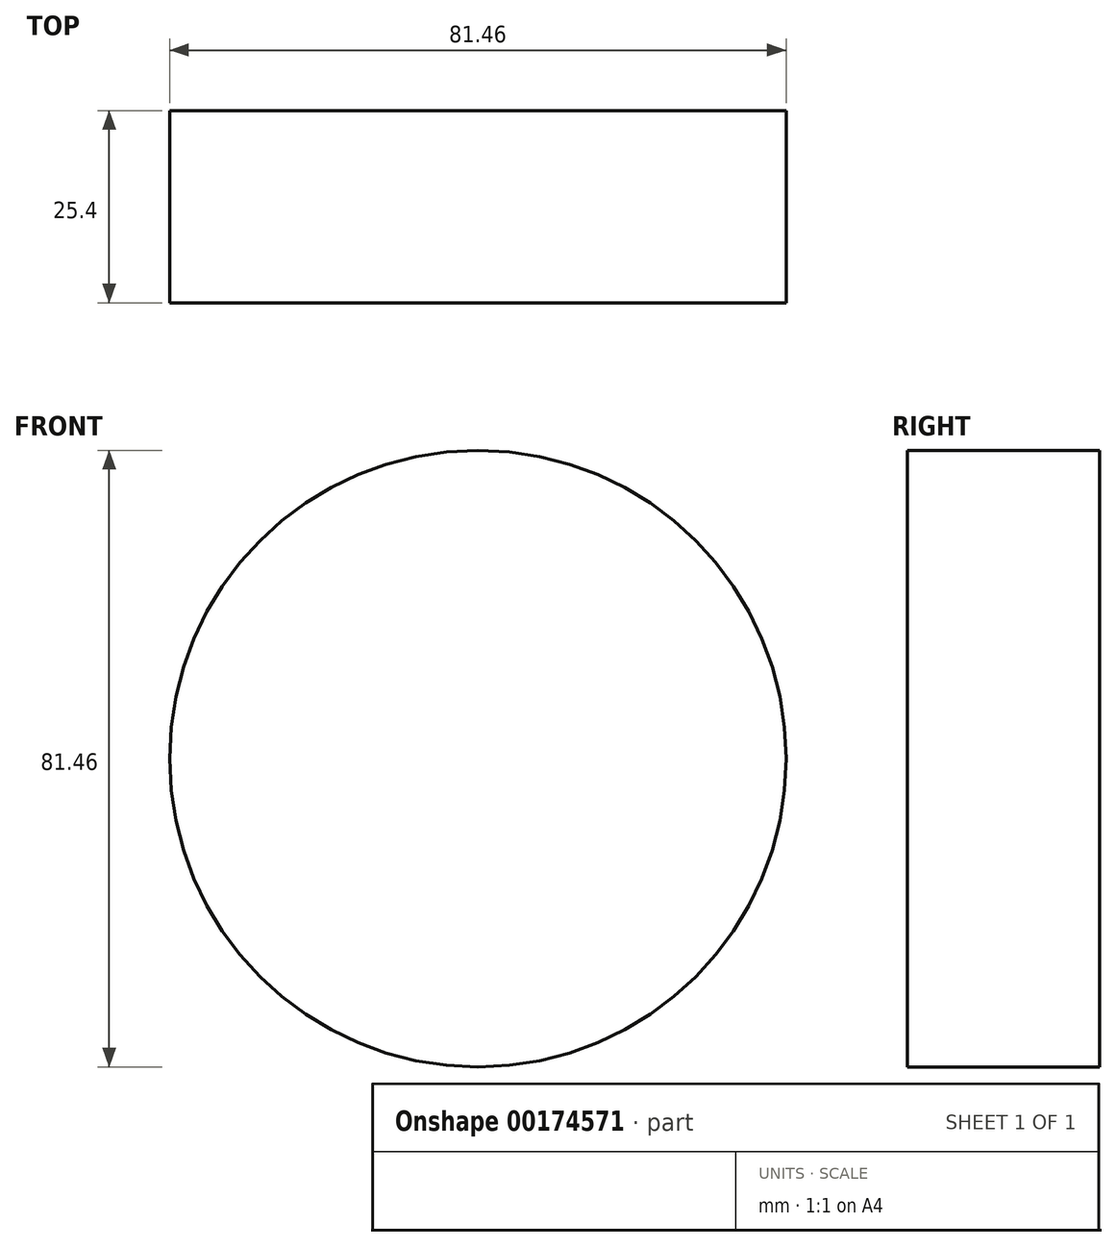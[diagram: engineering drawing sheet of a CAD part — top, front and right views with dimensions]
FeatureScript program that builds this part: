
annotation { "Feature Type Name" : "Feature", "Feature Type Description" : "" }
export const myFeature = defineFeature(function(context is Context, id is Id, definition is map)
    precondition{}
    {
        {
            var Q0;
            Q0=qCreatedBy(makeId("Front.planeOp"),FACE);
            var sketch = newSketch(context, id + "F0", { "sketchPlane" : qUnion([Q0])});
            skCircle(sketch, "E0", {"center": v(0, 0) * mm, "radius": 40.73 * mm});
            skSolve(sketch);
        }
        {
            var Q0;
            Q0=makeQuery(id+"F0.imprint","IMPRINT",FACE,{"disambiguationData":[TD([[makeQuery(id+"F0.imprint","IMPRINT",EDGE,{"derivedFrom":sQuery(id+"F0.wireOp",EDGE,"E0")}),1.0]])]});
            extrude(context, id + "F1", {"entities" : qUnion([Q0]), "depth" : 25.4 * mm});
        }
    });
